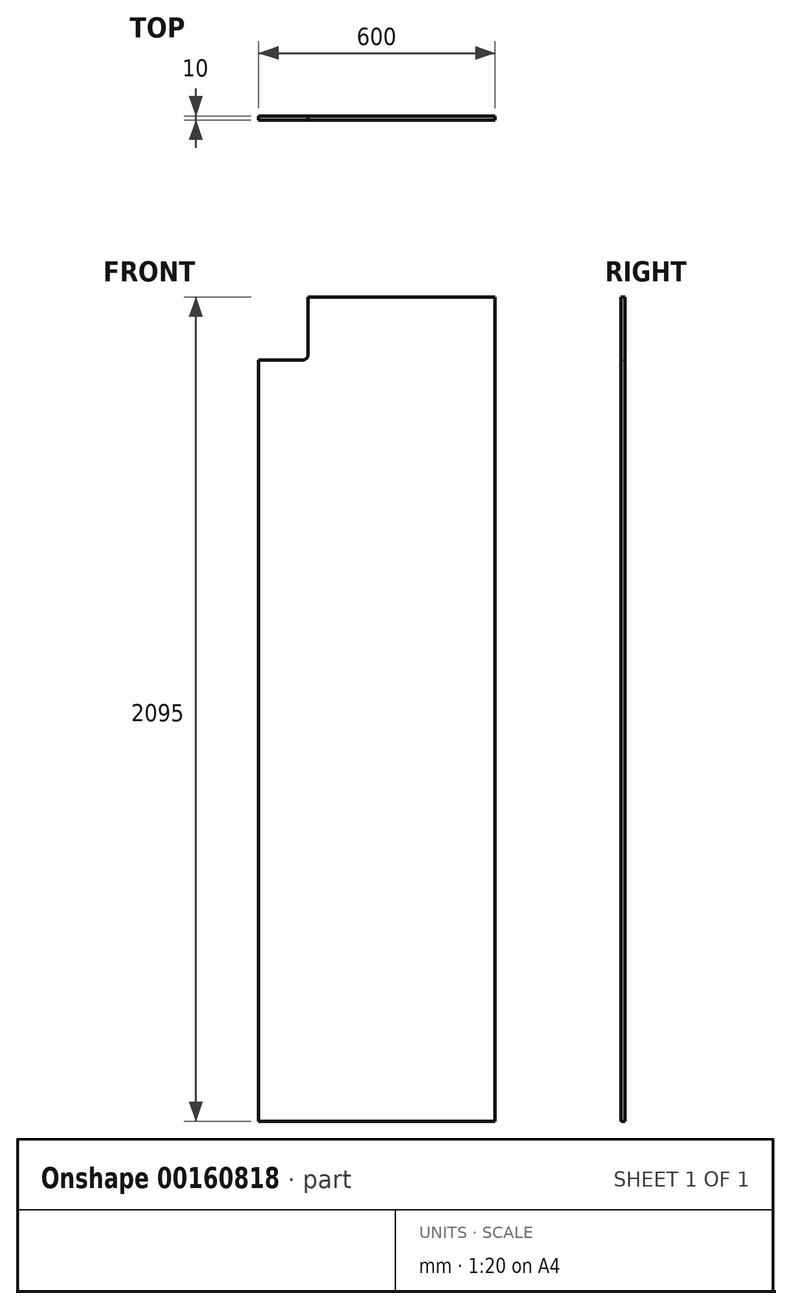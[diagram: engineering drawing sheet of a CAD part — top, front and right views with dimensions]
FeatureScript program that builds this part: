
annotation { "Feature Type Name" : "Feature", "Feature Type Description" : "" }
export const myFeature = defineFeature(function(context is Context, id is Id, definition is map)
    precondition{}
    {
        {
            var Q0;
            Q0=qCreatedBy(makeId("Front.planeOp"),FACE);
            var sketch = newSketch(context, id + "F0", { "sketchPlane" : qUnion([Q0])});
            skLineSegment(sketch, "E0.bottom", {"start": v(0, 0) * mm, "end": v(600, 0) * mm});
            skLineSegment(sketch, "E0.top", {"start": v(125, 2095) * mm, "end": v(600, 2095) * mm});
            skLineSegment(sketch, "E0.left", {"start": v(0, 0) * mm, "end": v(0, 1935) * mm});
            skLineSegment(sketch, "E0.right", {"start": v(600, 0) * mm, "end": v(600, 2095) * mm});
            skLineSegment(sketch, "E1.top", {"start": v(0, 1935) * mm, "end": v(112, 1935) * mm});
            skLineSegment(sketch, "E1.right", {"start": v(125, 2095) * mm, "end": v(125, 1948) * mm});
            skPoint(sketch, "E2.visualSharp", {"position": v(125, 1935) * mm});
            skArc(sketch, "E2.filletArc", {"start": v(112, 1935) * mm, "mid": v(121.2, 1938.8) * mm, "end": v(125, 1948) * mm});
            skSolve(sketch);
        }
        {
            var Q0;
            Q0=qSketchRegion(id+"F0",true);
            extrude(context, id + "F1", {"entities" : qUnion([Q0]), "depth" : 10 * mm});
        }
    });
